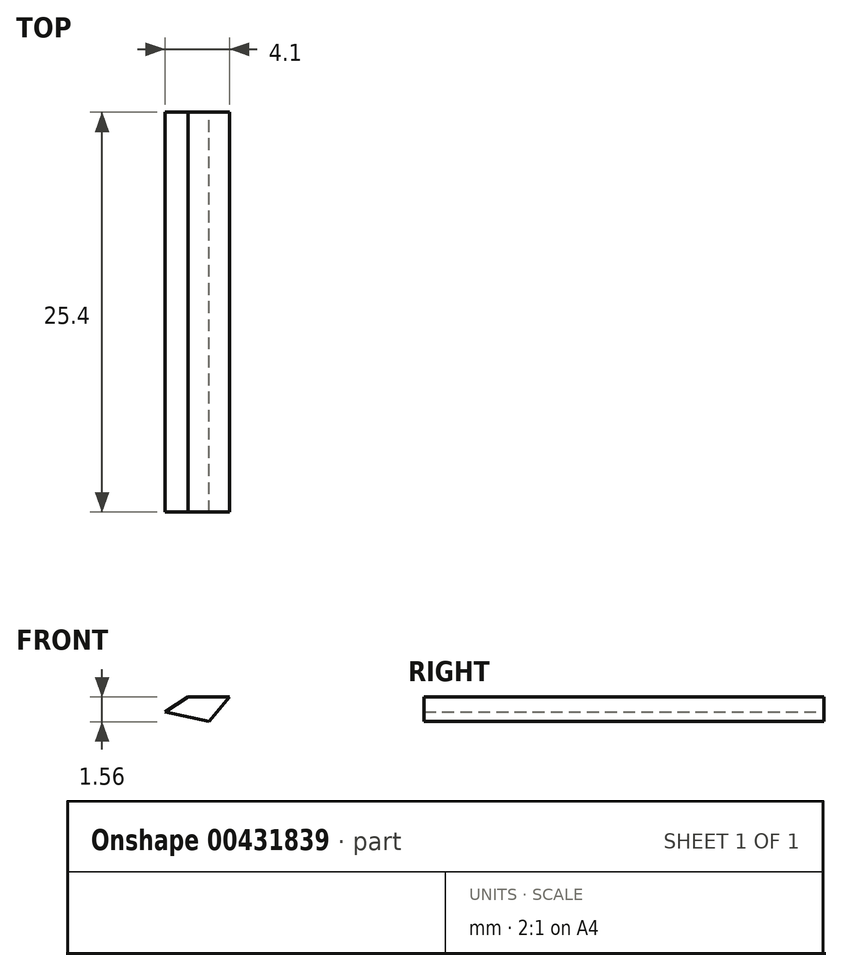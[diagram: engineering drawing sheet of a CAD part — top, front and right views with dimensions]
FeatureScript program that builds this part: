
annotation { "Feature Type Name" : "Feature", "Feature Type Description" : "" }
export const myFeature = defineFeature(function(context is Context, id is Id, definition is map)
    precondition{}
    {
        {
            var Q0;
            Q0=qCreatedBy(makeId("Front.planeOp"),FACE);
            var sketch = newSketch(context, id + "F0", { "sketchPlane" : qUnion([Q0])});
            skLineSegment(sketch, "E0", {"start": v(-63.2, 35.9) * mm, "end": v(-61.73, 36.83) * mm});
            skLineSegment(sketch, "E1", {"start": v(-61.73, 36.83) * mm, "end": v(-59.1, 36.83) * mm});
            skLineSegment(sketch, "E2", {"start": v(-59.1, 36.83) * mm, "end": v(-60.39, 35.27) * mm});
            skLineSegment(sketch, "E3", {"start": v(-60.39, 35.27) * mm, "end": v(-63.2, 35.9) * mm});
            skSolve(sketch);
        }
        {
            var Q0;
            Q0 = qSketchRegion(id + "F0", true);
            extrude(context, id + "F1", {"entities" : qUnion([Q0]), "depth" : 25.4 * mm});
        }
    });
